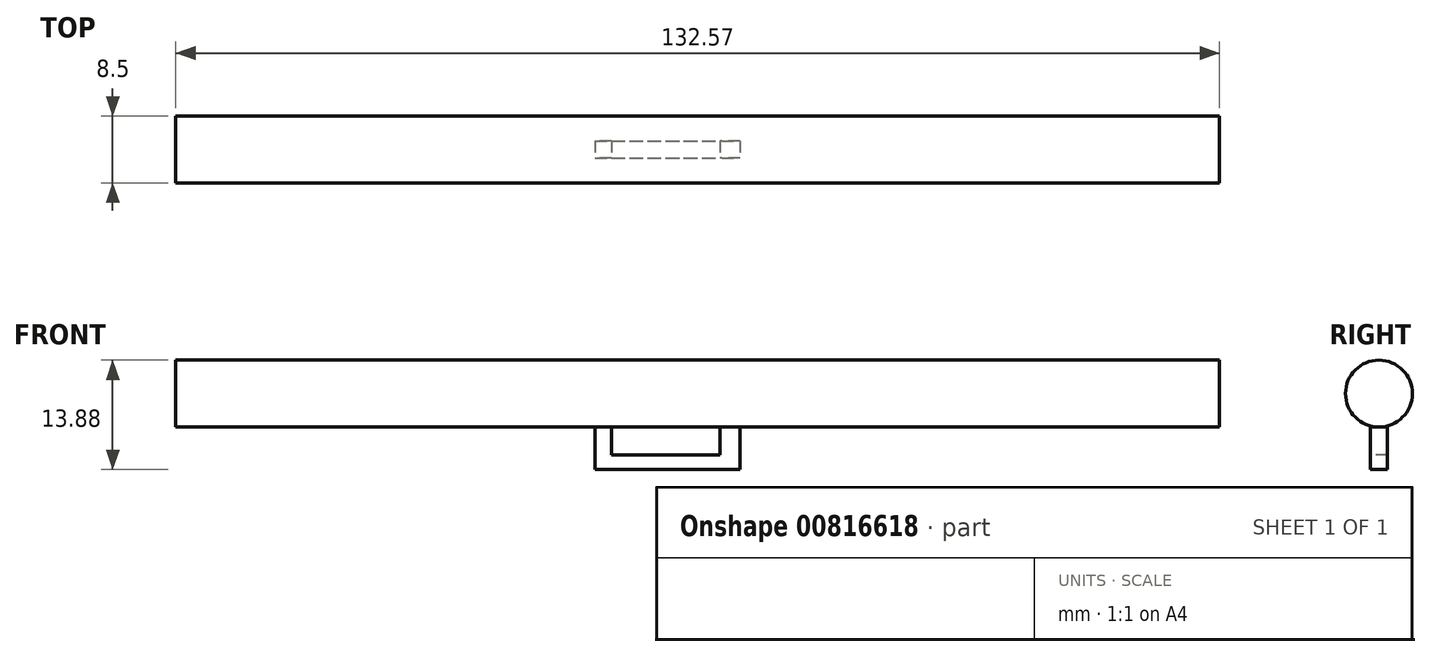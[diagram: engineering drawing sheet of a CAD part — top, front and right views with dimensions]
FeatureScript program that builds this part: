
annotation { "Feature Type Name" : "Feature", "Feature Type Description" : "" }
export const myFeature = defineFeature(function(context is Context, id is Id, definition is map)
    precondition{}
    {
        {
            var Q0;
            Q0=qCreatedBy(makeId("Front.planeOp"),FACE);
            var sketch = newSketch(context, id + "F0", { "sketchPlane" : qUnion([Q0])});
            skLineSegment(sketch, "E0", {"start": v(-63.03, 37.53) * mm, "end": v(69.54, 37.53) * mm});
            skLineSegment(sketch, "E1", {"start": v(69.54, 37.53) * mm, "end": v(69.54, 33.28) * mm});
            skLineSegment(sketch, "E2", {"start": v(69.54, 33.28) * mm, "end": v(-63.03, 33.28) * mm});
            skLineSegment(sketch, "E3", {"start": v(-63.03, 33.28) * mm, "end": v(-63.03, 37.53) * mm});
            skLineSegment(sketch, "E4", {"start": v(-9.77, 33.28) * mm, "end": v(-9.77, 27.9) * mm});
            skLineSegment(sketch, "E5", {"start": v(-9.77, 27.9) * mm, "end": v(8.64, 27.9) * mm});
            skLineSegment(sketch, "E6", {"start": v(8.64, 27.9) * mm, "end": v(8.64, 33.28) * mm});
            skLineSegment(sketch, "E7", {"start": v(-7.71, 33.28) * mm, "end": v(-7.71, 29.72) * mm});
            skLineSegment(sketch, "E8", {"start": v(-7.71, 29.72) * mm, "end": v(6.1, 29.72) * mm});
            skLineSegment(sketch, "E9", {"start": v(6.1, 29.72) * mm, "end": v(6.1, 33.28) * mm});
            skSolve(sketch);
        }
        {
            var Q0;
            Q0=makeQuery(id+"F0.imprint","IMPRINT",FACE,{"disambiguationData":[TD([[makeQuery(id+"F0.imprint","IMPRINT",EDGE,{"derivedFrom":sQuery(id+"F0.wireOp",EDGE,"E0")}),-1.0]])]});
            var Q1;
            Q1=sQuery(id+"F0.wireOp",EDGE,"E0");
            revolve(context, id + "F1", {"surfaceOperationType" : NewSurfaceOperationType.NEW, "entities" : qUnion([Q0]), "axis" : qUnion([Q1]), "revolveType" : RevolveType.FULL});
        }
        {
            var Q0;
            {var subQ0=sQuery(id+"F0.wireOp",EDGE,"E4");Q0=makeQuery(id+"F0.imprint","IMPRINT",FACE,{"disambiguationData":[TD([[makeQuery(id+"F0.imprint","IMPRINT",EDGE,{"derivedFrom":subQ0}),1.0]])]});}
            extrude(context, id + "F2", {"entities" : qUnion([Q0]), "operationType" : NewBodyOperationType.ADD, "endBound" : BoundingType.SYMMETRIC, "oppositeDirection" : true, "depth" : 2.2 * mm, "offsetDistance" : 25 * mm});
        }
        {
            var Q0;
            Q0=makeQuery(id+"F1.opRevolve","SWEPT_BODY",BODY,{"disambiguationData":[OSD([sQuery(id+"F0.wireOp",EDGE,"E0"),sQuery(id+"F0.wireOp",EDGE,"E1"),sQuery(id+"F0.wireOp",EDGE,"E2"),sQuery(id+"F0.wireOp",EDGE,"E3")])]});
            var Q1;
            Q1=makeQuery(id+"F2.opExtrude","SWEPT_BODY",BODY,{"disambiguationData":[OSD([sQuery(id+"F0.wireOp",EDGE,"E2"),sQuery(id+"F0.wireOp",EDGE,"E4"),sQuery(id+"F0.wireOp",EDGE,"E5"),sQuery(id+"F0.wireOp",EDGE,"E6"),sQuery(id+"F0.wireOp",EDGE,"E7"),sQuery(id+"F0.wireOp",EDGE,"E8"),sQuery(id+"F0.wireOp",EDGE,"E9")])]});
            var Q2;
            Q2=makeQuery(id+"F1.opRevolve","SWEPT_BODY",BODY,{"disambiguationData":[OSD([sQuery(id+"F0.wireOp",EDGE,"E0"),sQuery(id+"F0.wireOp",EDGE,"E1"),sQuery(id+"F0.wireOp",EDGE,"E2"),sQuery(id+"F0.wireOp",EDGE,"E3")])]});
            var Q3;
            Q3=makeQuery(id+"F2.opExtrude","SWEPT_BODY",BODY,{"disambiguationData":[OSD([sQuery(id+"F0.wireOp",EDGE,"E2"),sQuery(id+"F0.wireOp",EDGE,"E4"),sQuery(id+"F0.wireOp",EDGE,"E5"),sQuery(id+"F0.wireOp",EDGE,"E6"),sQuery(id+"F0.wireOp",EDGE,"E7"),sQuery(id+"F0.wireOp",EDGE,"E8"),sQuery(id+"F0.wireOp",EDGE,"E9")])]});
            booleanBodies(context, id + "F3", {"operationType" : BooleanOperationType.INTERSECTION, "tools" : qUnion([Q0, Q1]), "targets" : qUnion([Q2, Q3]), "keepTools" : true});
        }
    });
